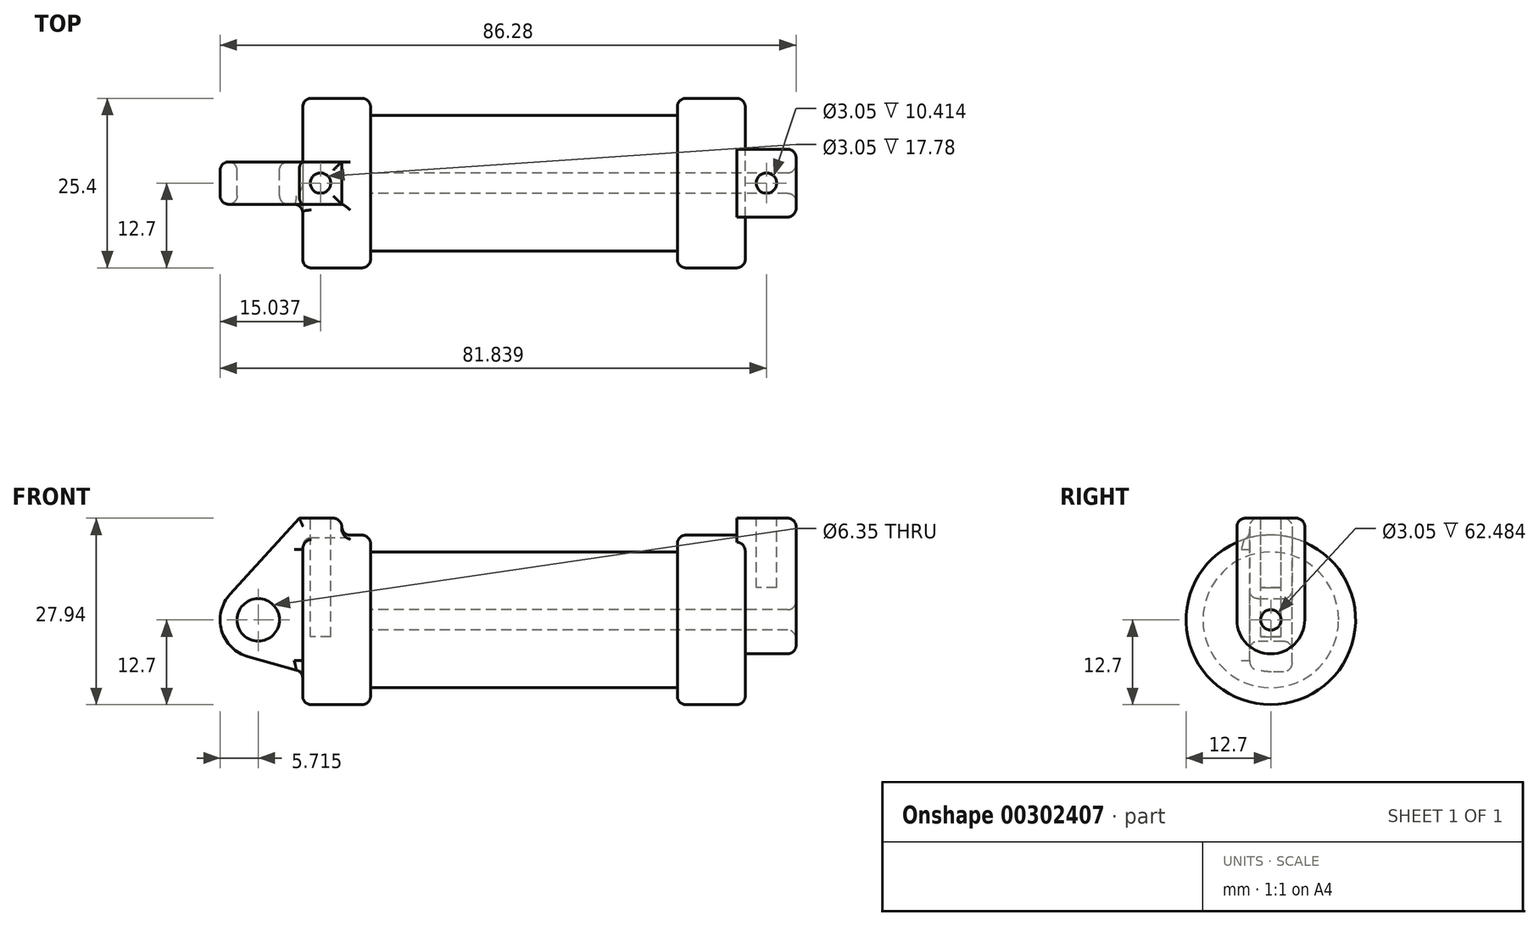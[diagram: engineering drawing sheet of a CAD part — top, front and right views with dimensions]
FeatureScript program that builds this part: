
annotation { "Feature Type Name" : "Feature", "Feature Type Description" : "" }
export const myFeature = defineFeature(function(context is Context, id is Id, definition is map)
    precondition{}
    {
        {
            var Q0;
            Q0=qCreatedBy(makeId("Front.planeOp"),FACE);
            var sketch = newSketch(context, id + "F0", { "sketchPlane" : qUnion([Q0])});
            skLineSegment(sketch, "E0", {"start": v(0, 0) * mm, "end": v(0, 12.7) * mm});
            skLineSegment(sketch, "E1", {"start": v(0, 12.7) * mm, "end": v(10.16, 12.7) * mm});
            skLineSegment(sketch, "E2", {"start": v(10.16, 12.7) * mm, "end": v(10.16, 10.16) * mm});
            skLineSegment(sketch, "E3", {"start": v(10.16, 10.16) * mm, "end": v(56.13, 10.16) * mm});
            skLineSegment(sketch, "E4", {"start": v(56.13, 10.16) * mm, "end": v(56.13, 12.7) * mm});
            skLineSegment(sketch, "E5", {"start": v(56.13, 12.7) * mm, "end": v(66.3, 12.7) * mm});
            skLineSegment(sketch, "E6", {"start": v(66.3, 12.7) * mm, "end": v(66.3, 0) * mm});
            skLineSegment(sketch, "E7", {"start": v(66.3, 0) * mm, "end": v(0, 0) * mm});
            skLineSegment(sketch, "E8", {"start": v(5.84, 15.24) * mm, "end": v(-0.5, 15.24) * mm});
            skLineSegment(sketch, "E9", {"start": v(-0.5, 15.24) * mm, "end": v(-10.88, 3.85) * mm});
            skLineSegment(sketch, "E10", {"start": v(0, 0) * mm, "end": v(-6.65, 0) * mm});
            skCircle(sketch, "E11", {"center": v(-6.65, 0) * mm, "radius": 5.72 * mm});
            skCircle(sketch, "E12", {"center": v(-6.65, 0) * mm, "radius": 3.18 * mm});
            skLineSegment(sketch, "E13", {"start": v(5.84, 15.24) * mm, "end": v(5.84, -9.4) * mm});
            skLineSegment(sketch, "E14", {"start": v(5.84, -9.4) * mm, "end": v(-8.18, -5.5) * mm});
            skSolve(sketch);
        }
        {
            var Q0;
            {var subQ0=sQuery(id+"F0.wireOp",EDGE,"E2");Q0=makeQuery(id+"F0.imprint","IMPRINT",FACE,{"disambiguationData":[TD([[makeQuery(id+"F0.imprint","IMPRINT",EDGE,{"derivedFrom":subQ0}),-1.0]])]});}
            var Q1;
            {var subQ0=sQuery(id+"F0.wireOp",EDGE,"E0");Q1=makeQuery(id+"F0.imprint","IMPRINT",FACE,{"disambiguationData":[TD([[makeQuery(id+"F0.imprint","IMPRINT",EDGE,{"derivedFrom":subQ0}),-1.0]])]});}
            var Q2;
            Q2=sQuery(id+"F0.wireOp",EDGE,"E7");
            revolve(context, id + "F1", {"entities" : qUnion([Q0, Q1]), "axis" : qUnion([Q2]), "revolveType" : RevolveType.FULL, "oppositeDirection" : true});
        }
        {
            var Q0;
            {var subQ5=sQuery(id+"F0.wireOp",EDGE,"E12");Q0=makeQuery(id+"F0.imprint","IMPRINT",FACE,{"disambiguationData":[TD([[makeQuery(id+"F0.imprint","IMPRINT",EDGE,{"derivedFrom":subQ5}),-1.0]])]});}
            var Q1;
            {var subQ1=sQuery(id+"F0.wireOp",EDGE,"E0");Q1=makeQuery(id+"F0.imprint","IMPRINT",FACE,{"disambiguationData":[TD([[makeQuery(id+"F0.imprint","IMPRINT",EDGE,{"derivedFrom":subQ1}),1.0]])]});}
            var Q2;
            {var subQ0=sQuery(id+"F0.wireOp",EDGE,"E0");Q2=makeQuery(id+"F0.imprint","IMPRINT",FACE,{"disambiguationData":[TD([[makeQuery(id+"F0.imprint","IMPRINT",EDGE,{"derivedFrom":subQ0}),-1.0]])]});}
            var Q3;
            {var subQ0=sQuery(id+"F0.wireOp",EDGE,"E14");Q3=makeQuery(id+"F0.imprint","IMPRINT",FACE,{"disambiguationData":[TD([[makeQuery(id+"F0.imprint","IMPRINT",EDGE,{"derivedFrom":subQ0}),-1.0]])]});}
            extrude(context, id + "F2", {"entities" : qUnion([Q0, Q1, Q2, Q3]), "operationType" : NewBodyOperationType.ADD, "endBound" : BoundingType.SYMMETRIC, "depth" : 6.35 * mm});
        }
        {
            var Q0;
            Q0=makeQuery(id+"F1.opRevolve","SWEPT_FACE",FACE,{"disambiguationData":[OSD([sQuery(id+"F0.wireOp",EDGE,"E6")])]});
            var sketch = newSketch(context, id + "F3", { "sketchPlane" : qUnion([Q0])});
            skCircle(sketch, "E15", {"center": v(0, 0) * mm, "radius": 1.52 * mm});
            skCircle(sketch, "E16", {"center": v(0, 0) * mm, "radius": 5.08 * mm});
            skLineSegment(sketch, "E17", {"start": v(-5.08, 0) * mm, "end": v(-5.08, 15.24) * mm});
            skLineSegment(sketch, "E18", {"start": v(-5.08, 15.24) * mm, "end": v(5.08, 15.24) * mm});
            skLineSegment(sketch, "E19", {"start": v(5.08, 15.24) * mm, "end": v(5.08, 0) * mm});
            skSolve(sketch);
        }
        {
            var Q0;
            Q0 = qSketchRegion(id + "F3", true);
            extrude(context, id + "F4", {"entities" : qUnion([Q0]), "operationType" : NewBodyOperationType.ADD, "oppositeDirection" : true, "depth" : 1.27 * mm});
        }
        {
            var Q0;
            Q0 = qSketchRegion(id + "F3", true);
            extrude(context, id + "F5", {"entities" : qUnion([Q0]), "operationType" : NewBodyOperationType.ADD, "depth" : 7.62 * mm});
        }
        {
            var Q0;
            {var subQ0=sQuery(id+"F3.wireOp",EDGE,"E15");Q0=makeQuery(id+"F5.boolean.opBoolean","SPLIT",FACE,{"disambiguationData":[TD([makeQuery(id+"F5.opExtrude","SWEPT_FACE",FACE,{"disambiguationData":[OSD([subQ0])]})])],"derivedFrom":makeQuery(id+"F4.boolean.opBoolean","MERGE",FACE,{"derivedFrom":[makeQuery(id+"F1.opRevolve","SWEPT_FACE",FACE,{"disambiguationData":[OSD([sQuery(id+"F0.wireOp",EDGE,"E6")])]}),makeQuery(id+"F4.opExtrude","CAP_FACE",FACE,{"disambiguationData":[OSD([subQ0,sQuery(id+"F3.wireOp",EDGE,"E16"),sQuery(id+"F3.wireOp",EDGE,"E17"),sQuery(id+"F3.wireOp",EDGE,"E18"),sQuery(id+"F3.wireOp",EDGE,"E19")])],"isStart":true})]})});}
            var Q1;
            Q1=makeQuery(id+"F1.opRevolve","SWEPT_FACE",FACE,{"disambiguationData":[OSD([sQuery(id+"F0.wireOp",EDGE,"E2")])]});
            extrude(context, id + "F6", {"entities" : qUnion([Q0]), "operationType" : NewBodyOperationType.REMOVE, "endBound" : BoundingType.UP_TO_SURFACE, "oppositeDirection" : true, "endBoundEntityFace" : qUnion([Q1]), "depth" : 57.15 * mm});
        }
        {
            var Q0;
            {var subQ0=sQuery(id+"F3.wireOp",EDGE,"E18");Q0=makeQuery(id+"F5.boolean.opBoolean","MERGE",FACE,{"derivedFrom":[makeQuery(id+"F4.opExtrude","SWEPT_FACE",FACE,{"disambiguationData":[OSD([subQ0])]}),makeQuery(id+"F5.opExtrude","SWEPT_FACE",FACE,{"disambiguationData":[OSD([subQ0])]})]});}
            var sketch = newSketch(context, id + "F7", { "sketchPlane" : qUnion([Q0])});
            skCircle(sketch, "E20", {"center": v(69.47, 0) * mm, "radius": 1.52 * mm});
            skPoint(sketch, "E20.centerSnap0", {"position": v(65.02, 0) * mm});
            skSolve(sketch);
        }
        {
            var Q0;
            Q0=makeQuery(id+"F7.imprint","IMPRINT",FACE,{"disambiguationData":[TD([[makeQuery(id+"F7.imprint","IMPRINT",EDGE,{"derivedFrom":sQuery(id+"F7.wireOp",EDGE,"E20")}),1.0]])]});
            extrude(context, id + "F8", {"entities" : qUnion([Q0]), "operationType" : NewBodyOperationType.REMOVE, "oppositeDirection" : true, "depth" : 10.4 * mm});
        }
        {
            var Q0;
            Q0=makeQuery(id+"F2.opExtrude","SWEPT_FACE",FACE,{"disambiguationData":[OSD([sQuery(id+"F0.wireOp",EDGE,"E8")])]});
            var sketch = newSketch(context, id + "F9", { "sketchPlane" : qUnion([Q0])});
            skCircle(sketch, "E21", {"center": v(2.67, 0) * mm, "radius": 1.52 * mm});
            skSolve(sketch);
        }
        {
            var Q0;
            Q0=makeQuery(id+"F9.imprint","IMPRINT",FACE,{"disambiguationData":[TD([[makeQuery(id+"F9.imprint","IMPRINT",EDGE,{"derivedFrom":sQuery(id+"F9.wireOp",EDGE,"E21")}),1.0]])]});
            extrude(context, id + "F10", {"entities" : qUnion([Q0]), "operationType" : NewBodyOperationType.REMOVE, "oppositeDirection" : true, "depth" : 17.78 * mm});
        }
        {
            var Q0;
            Q0=makeQuery(id+"F1.opRevolve","SWEPT_EDGE",EDGE,{"disambiguationData":[OSD([sQuery(id+"F0.wireOp",EDGE,"E0"),sQuery(id+"F0.wireOp",EDGE,"E1")])]});
            var Q1;
            Q1=makeQuery(id+"F1.opRevolve","SWEPT_EDGE",EDGE,{"disambiguationData":[OSD([sQuery(id+"F0.wireOp",EDGE,"E1"),sQuery(id+"F0.wireOp",EDGE,"E2")])]});
            var Q2;
            Q2=makeQuery(id+"F1.opRevolve","SWEPT_EDGE",EDGE,{"disambiguationData":[OSD([sQuery(id+"F0.wireOp",EDGE,"E4"),sQuery(id+"F0.wireOp",EDGE,"E5")])]});
            var Q3;
            Q3=makeQuery(id+"F1.opRevolve","SWEPT_EDGE",EDGE,{"disambiguationData":[OSD([sQuery(id+"F0.wireOp",EDGE,"E5"),sQuery(id+"F0.wireOp",EDGE,"E6")])]});
            fillet(context, id + "F11", {"entities" : qUnion([Q0, Q1, Q2, Q3]), "radius" : 1.27 * mm, "tangentPropagation" : true, "allowEdgeOverflow" : false});
        }
        {
            var Q0;
            {var subQ0=sQuery(id+"F3.wireOp",EDGE,"E18");var subQ1=sQuery(id+"F3.wireOp",EDGE,"E17");Q0=makeQuery(id+"F5.boolean.opBoolean","MERGE",EDGE,{"derivedFrom":[makeQuery(id+"F4.opExtrude","SWEPT_EDGE",EDGE,{"disambiguationData":[OSD([subQ1,subQ0])]}),makeQuery(id+"F5.opExtrude","SWEPT_EDGE",EDGE,{"disambiguationData":[OSD([subQ1,subQ0])]})]});}
            var Q1;
            Q1=makeQuery(id+"F5.opExtrude","CAP_EDGE",EDGE,{"disambiguationData":[OSD([sQuery(id+"F3.wireOp",EDGE,"E17")])],"isStart":true});
            var Q2;
            Q2=makeQuery(id+"F5.opExtrude","CAP_EDGE",EDGE,{"disambiguationData":[OSD([sQuery(id+"F3.wireOp",EDGE,"E17")])],"isStart":false});
            var Q3;
            Q3=makeQuery(id+"F5.opExtrude","CAP_EDGE",EDGE,{"disambiguationData":[OSD([sQuery(id+"F3.wireOp",EDGE,"E18")])],"isStart":false});
            var Q4;
            {var subQ0=sQuery(id+"F3.wireOp",EDGE,"E19");var subQ1=sQuery(id+"F3.wireOp",EDGE,"E18");Q4=makeQuery(id+"F5.boolean.opBoolean","MERGE",EDGE,{"derivedFrom":[makeQuery(id+"F4.opExtrude","SWEPT_EDGE",EDGE,{"disambiguationData":[OSD([subQ1,subQ0])]}),makeQuery(id+"F5.opExtrude","SWEPT_EDGE",EDGE,{"disambiguationData":[OSD([subQ1,subQ0])]})]});}
            var Q5;
            Q5=makeQuery(id+"F8.boolean.opBoolean","COPY",EDGE,{"derivedFrom":makeQuery(id+"F8.opExtrude","CAP_EDGE",EDGE,{"disambiguationData":[OSD([sQuery(id+"F7.wireOp",EDGE,"E20")])],"isStart":true})});
            var Q6;
            Q6=makeQuery(id+"F5.opExtrude","CAP_EDGE",EDGE,{"disambiguationData":[OSD([sQuery(id+"F3.wireOp",EDGE,"E15")])],"isStart":false});
            fillet(context, id + "F12", {"entities" : qUnion([Q0, Q1, Q2, Q3, Q4, Q5, Q6]), "radius" : 1.27 * mm, "tangentPropagation" : true, "allowEdgeOverflow" : false});
        }
        {
            var Q0;
            Q0=makeQuery(id+"F10.boolean.opBoolean","COPY",EDGE,{"derivedFrom":makeQuery(id+"F10.opExtrude","CAP_EDGE",EDGE,{"disambiguationData":[OSD([sQuery(id+"F9.wireOp",EDGE,"E21")])],"isStart":true})});
            var Q1;
            Q1=makeQuery(id+"F2.opExtrude","CAP_EDGE",EDGE,{"disambiguationData":[OSD([sQuery(id+"F0.wireOp",EDGE,"E12")])],"isStart":false});
            var Q2;
            Q2=makeQuery(id+"F2.opExtrude","CAP_EDGE",EDGE,{"disambiguationData":[OSD([sQuery(id+"F0.wireOp",EDGE,"E12")])],"isStart":true});
            var Q3;
            Q3=makeQuery(id+"F2.opExtrude","CAP_EDGE",EDGE,{"disambiguationData":[OSD([sQuery(id+"F0.wireOp",EDGE,"E9")])],"isStart":true});
            var Q4;
            Q4=makeQuery(id+"F2.opExtrude","CAP_EDGE",EDGE,{"disambiguationData":[OSD([sQuery(id+"F0.wireOp",EDGE,"E9")])],"isStart":false});
            var Q5;
            Q5=makeQuery(id+"F2.opExtrude","CAP_EDGE",EDGE,{"disambiguationData":[OSD([sQuery(id+"F0.wireOp",EDGE,"E8")])],"isStart":false});
            var Q6;
            Q6=makeQuery(id+"F2.opExtrude","SWEPT_EDGE",EDGE,{"disambiguationData":[OSD([sQuery(id+"F0.wireOp",EDGE,"E8"),sQuery(id+"F0.wireOp",EDGE,"E13")])]});
            var Q7;
            Q7=makeQuery(id+"F2.opExtrude","CAP_EDGE",EDGE,{"disambiguationData":[OSD([sQuery(id+"F0.wireOp",EDGE,"E8")])],"isStart":true});
            var Q8;
            Q8=makeQuery(id+"F2.boolean.opBoolean","INTERSECT",EDGE,{"derivedFrom":[makeQuery(id+"F1.opRevolve","SWEPT_FACE",FACE,{"disambiguationData":[OSD([sQuery(id+"F0.wireOp",EDGE,"E1")])]}),makeQuery(id+"F2.opExtrude","SWEPT_FACE",FACE,{"disambiguationData":[OSD([sQuery(id+"F0.wireOp",EDGE,"E13")])]})]});
            var Q9;
            Q9=makeQuery(id+"F2.boolean.opBoolean","INTERSECT",EDGE,{"derivedFrom":[makeQuery(id+"F1.opRevolve","SWEPT_FACE",FACE,{"disambiguationData":[OSD([sQuery(id+"F0.wireOp",EDGE,"E1")])]}),makeQuery(id+"F2.opExtrude","CAP_FACE",FACE,{"disambiguationData":[OSD([sQuery(id+"F0.wireOp",EDGE,"E8"),sQuery(id+"F0.wireOp",EDGE,"E9"),sQuery(id+"F0.wireOp",EDGE,"E11"),sQuery(id+"F0.wireOp",EDGE,"E12"),sQuery(id+"F0.wireOp",EDGE,"E13"),sQuery(id+"F0.wireOp",EDGE,"E14")])],"isStart":false})]});
            fillet(context, id + "F13", {"entities" : qUnion([Q0, Q1, Q2, Q3, Q4, Q5, Q6, Q7, Q8, Q9]), "radius" : 1.27 * mm, "tangentPropagation" : true, "allowEdgeOverflow" : false});
        }
    });
